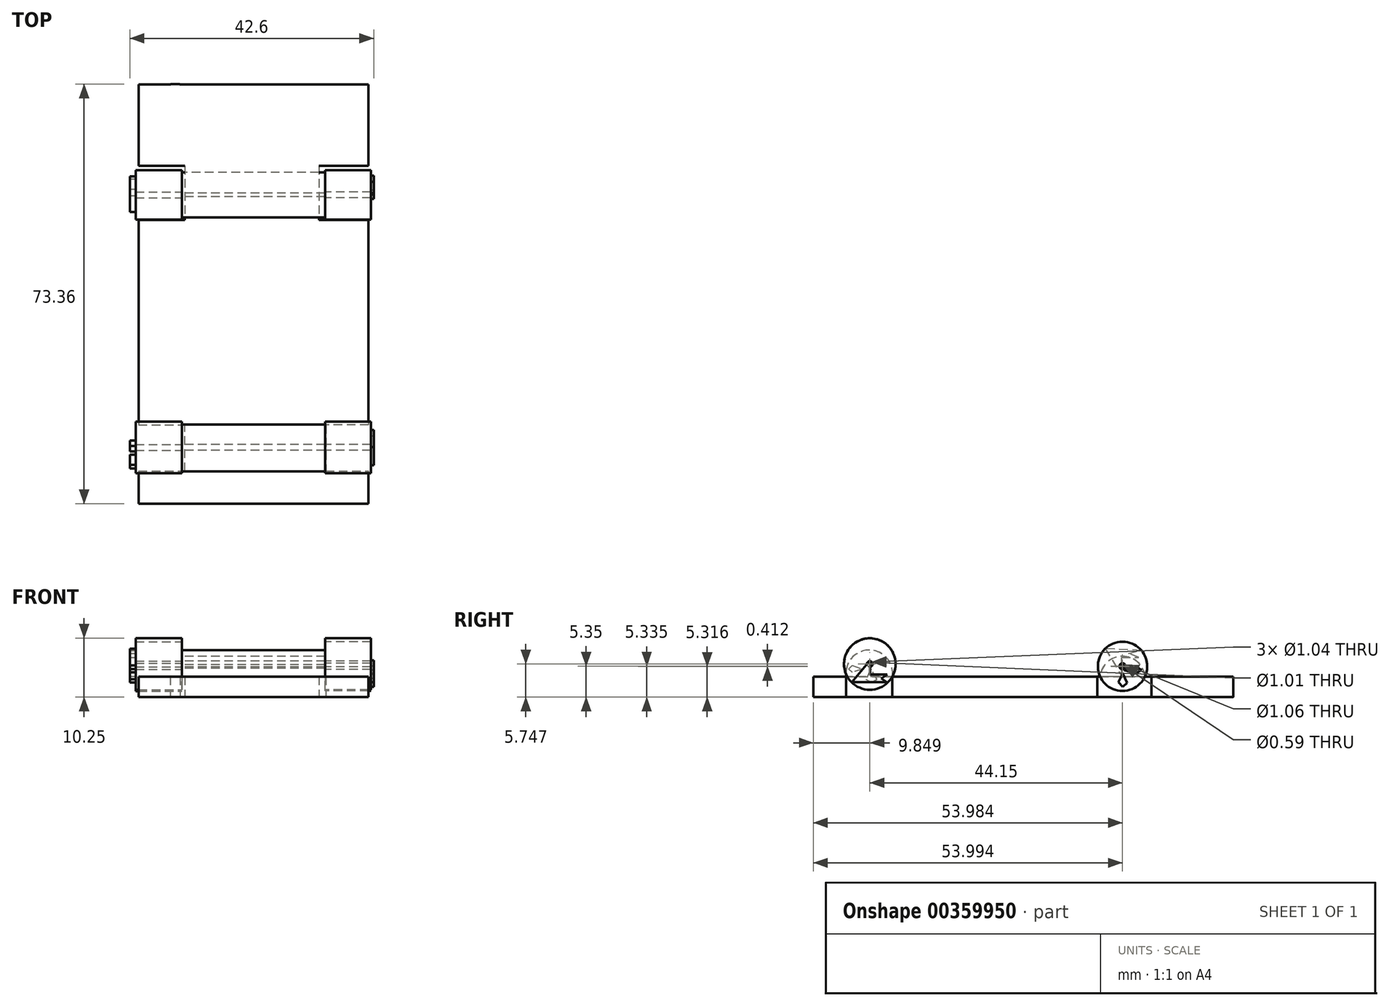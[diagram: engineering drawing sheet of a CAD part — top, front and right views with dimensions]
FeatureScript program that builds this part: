
annotation { "Feature Type Name" : "Feature", "Feature Type Description" : "" }
export const myFeature = defineFeature(function(context is Context, id is Id, definition is map)
    precondition{}
    {
        {
            var Q0;
            Q0=qCreatedBy(makeId("Top.planeOp"),FACE);
            var sketch = newSketch(context, id + "F0", { "sketchPlane" : qUnion([Q0])});
            skLineSegment(sketch, "E0.bottom", {"start": v(-14.53, 35.08) * mm, "end": v(14.97, 35.08) * mm});
            skLineSegment(sketch, "E0.top", {"start": v(-15.4, -38.23) * mm, "end": v(16.36, -38.23) * mm});
            skLineSegment(sketch, "E0.left", {"start": v(-20.07, 31.05) * mm, "end": v(-20.07, 20.84) * mm});
            skLineSegment(sketch, "E0.right", {"start": v(20.1, 30.52) * mm, "end": v(20.1, 20.84) * mm});
            skLineSegment(sketch, "E1", {"start": v(-20.07, 20.84) * mm, "end": v(-12.02, 20.84) * mm});
            skLineSegment(sketch, "E2", {"start": v(-12.02, 20.84) * mm, "end": v(-12.02, 11.39) * mm});
            skLineSegment(sketch, "E3", {"start": v(-20.07, 11.39) * mm, "end": v(-12.02, 11.39) * mm});
            skLineSegment(sketch, "E4", {"start": v(-20.07, -24.44) * mm, "end": v(-12.02, -24.44) * mm});
            skLineSegment(sketch, "E5", {"start": v(-12.02, -32.52) * mm, "end": v(-12.02, -24.44) * mm});
            skLineSegment(sketch, "E6", {"start": v(-20.07, -32.52) * mm, "end": v(-12.02, -32.52) * mm});
            skLineSegment(sketch, "E7", {"start": v(20.1, 20.84) * mm, "end": v(11.43, 20.84) * mm});
            skLineSegment(sketch, "E8", {"start": v(11.43, 20.84) * mm, "end": v(11.43, 11.39) * mm});
            skLineSegment(sketch, "E9", {"start": v(11.43, 11.39) * mm, "end": v(20.1, 11.39) * mm});
            skLineSegment(sketch, "E10", {"start": v(20.1, -24.44) * mm, "end": v(12.61, -24.44) * mm});
            skLineSegment(sketch, "E11", {"start": v(12.61, -24.44) * mm, "end": v(12.61, -32.52) * mm});
            skLineSegment(sketch, "E12", {"start": v(12.61, -32.52) * mm, "end": v(20.1, -32.52) * mm});
            skLineSegment(sketch, "E13.trimOffspring", {"start": v(-20.07, 11.39) * mm, "end": v(-20.07, -24.44) * mm});
            skLineSegment(sketch, "E14.trimOffspring", {"start": v(-20.07, -32.52) * mm, "end": v(-20.07, -35.37) * mm});
            skLineSegment(sketch, "E15.trimOffspring", {"start": v(20.1, -32.52) * mm, "end": v(20.1, -35.37) * mm});
            skLineSegment(sketch, "E16.trimOffspring", {"start": v(20.1, 11.39) * mm, "end": v(20.1, -24.44) * mm});
            skArc(sketch, "E17", {"start": v(-12.82, 35.08) * mm, "mid": v(-13.68, 35.13) * mm, "end": v(-14.53, 35.08) * mm});
            skPoint(sketch, "E18.startSnap0", {"position": v(16.36, -24.44) * mm});
            skPoint(sketch, "E19.orphan", {"position": v(-20.07, -38.23) * mm});
            skPoint(sketch, "E20.orphan", {"position": v(20.1, -38.23) * mm});
            skLineSegment(sketch, "E21", {"start": v(-20.07, 31.05) * mm, "end": v(-20.07, 35.08) * mm});
            skLineSegment(sketch, "E22", {"start": v(-20.07, 35.08) * mm, "end": v(-14.53, 35.08) * mm});
            skLineSegment(sketch, "E23", {"start": v(14.97, 35.08) * mm, "end": v(20.1, 35.08) * mm});
            skLineSegment(sketch, "E24", {"start": v(20.1, 35.08) * mm, "end": v(20.1, 30.52) * mm});
            skLineSegment(sketch, "E25", {"start": v(-20.07, -35.37) * mm, "end": v(-20.07, -38.23) * mm});
            skLineSegment(sketch, "E26", {"start": v(-20.07, -38.23) * mm, "end": v(-15.4, -38.23) * mm});
            skLineSegment(sketch, "E27", {"start": v(16.36, -38.23) * mm, "end": v(20.1, -38.23) * mm});
            skLineSegment(sketch, "E28", {"start": v(20.1, -35.37) * mm, "end": v(20.1, -38.23) * mm});
            skSolve(sketch);
        }
        {
            var Q0;
            Q0 = qSketchRegion(id + "F0", true);
            extrude(context, id + "F1", {"entities" : qUnion([Q0]), "depth" : 3.56 * mm});
        }
        {
            var Q0;
            Q0=qCreatedBy(makeId("Right.planeOp"),FACE);
            var sketch = newSketch(context, id + "F2", { "sketchPlane" : qUnion([Q0])});
            skArc(sketch, "E29", {"start": v(-24.43, 3.56) * mm, "mid": v(-28.47, 8.2) * mm, "end": v(-32.52, 3.56) * mm});
            skArc(sketch, "E30", {"start": v(19.7, 3.55) * mm, "mid": v(15.77, 7.1) * mm, "end": v(11.82, 3.56) * mm});
            skLineSegment(sketch, "E31", {"start": v(-32.52, 3.56) * mm, "end": v(-24.43, 3.56) * mm});
            skCircle(sketch, "E32", {"center": v(-28.38, 5.75) * mm, "radius": 0.52 * mm});
            skCircle(sketch, "E33", {"center": v(15.75, 5.32) * mm, "radius": 0.3 * mm});
            skLineSegment(sketch, "E34", {"start": v(11.82, 3.56) * mm, "end": v(19.7, 3.55) * mm});
            skSolve(sketch);
        }
        {
            var Q0;
            Q0 = qSketchRegion(id + "F2", true);
            extrude(context, id + "F3", {"entities" : qUnion([Q0]), "endBound" : BoundingType.SYMMETRIC, "depth" : 25 * mm});
        }
        {
            var Q0;
            Q0=makeQuery(id+"F3.opExtrude","CAP_FACE",FACE,{"disambiguationData":[OSD([sQuery(id+"F2.wireOp",EDGE,"E29"),sQuery(id+"F2.wireOp",EDGE,"E31"),sQuery(id+"F2.wireOp",EDGE,"E32")])],"isStart":false});
            var sketch = newSketch(context, id + "F4", { "sketchPlane" : qUnion([Q0])});
            skCircle(sketch, "E35", {"center": v(-28.38, 5.75) * mm, "radius": 4.5 * mm});
            skCircle(sketch, "E36", {"center": v(15.76, 5.35) * mm, "radius": 4.3 * mm});
            skCircle(sketch, "E37", {"center": v(-28.38, 5.75) * mm, "radius": 0.5 * mm});
            skCircle(sketch, "E38", {"center": v(15.76, 5.35) * mm, "radius": 0.53 * mm});
            skSolve(sketch);
        }
        {
            var Q0;
            Q0 = qSketchRegion(id + "F4", true);
            extrude(context, id + "F5", {"entities" : qUnion([Q0]), "depth" : 8 * mm});
        }
        {
            var Q0;
            Q0=makeQuery(id+"F3.opExtrude","CAP_FACE",FACE,{"disambiguationData":[OSD([sQuery(id+"F2.wireOp",EDGE,"E29"),sQuery(id+"F2.wireOp",EDGE,"E31"),sQuery(id+"F2.wireOp",EDGE,"E32")])],"isStart":true});
            var sketch = newSketch(context, id + "F6", { "sketchPlane" : qUnion([Q0])});
            skCircle(sketch, "E39", {"center": v(28.38, 5.75) * mm, "radius": 4.5 * mm});
            skCircle(sketch, "E40", {"center": v(-15.77, 5.34) * mm, "radius": 4.31 * mm});
            skCircle(sketch, "E41", {"center": v(-15.77, 5.34) * mm, "radius": 0.52 * mm});
            skCircle(sketch, "E42", {"center": v(28.38, 5.75) * mm, "radius": 0.52 * mm});
            skSolve(sketch);
        }
        {
            var Q0;
            Q0 = qSketchRegion(id + "F6", true);
            extrude(context, id + "F7", {"entities" : qUnion([Q0]), "depth" : 8.1 * mm});
        }
        {
            var Q0;
            Q0=makeQuery(id+"F7.opExtrude","CAP_FACE",FACE,{"disambiguationData":[OSD([sQuery(id+"F6.wireOp",EDGE,"E39")])],"isStart":false});
            var sketch = newSketch(context, id + "F8", { "sketchPlane" : qUnion([Q0])});
            skLineSegment(sketch, "E43", {"start": v(31.43, 4.28) * mm, "end": v(32.05, 4.86) * mm});
            skLineSegment(sketch, "E44", {"start": v(32.05, 4.86) * mm, "end": v(31.44, 5.5) * mm});
            skLineSegment(sketch, "E45", {"start": v(31.44, 5.5) * mm, "end": v(29.64, 4.86) * mm});
            skLineSegment(sketch, "E46", {"start": v(29.64, 4.86) * mm, "end": v(31.43, 4.28) * mm});
            skLineSegment(sketch, "E47", {"start": v(28.13, 4.86) * mm, "end": v(29.1, 3.07) * mm});
            skLineSegment(sketch, "E48", {"start": v(29.1, 3.07) * mm, "end": v(28.07, 2.5) * mm});
            skLineSegment(sketch, "E49", {"start": v(28.07, 2.5) * mm, "end": v(27.15, 3.07) * mm});
            skLineSegment(sketch, "E50", {"start": v(27.15, 3.07) * mm, "end": v(28.13, 4.86) * mm});
            skLineSegment(sketch, "E51", {"start": v(-18.99, 8.14) * mm, "end": v(-12.76, 8.42) * mm});
            skLineSegment(sketch, "E52", {"start": v(-12.76, 8.42) * mm, "end": v(-15.63, 3.6) * mm});
            skLineSegment(sketch, "E53", {"start": v(-15.63, 3.6) * mm, "end": v(-15.63, 6.9) * mm});
            skLineSegment(sketch, "E54", {"start": v(-15.63, 6.9) * mm, "end": v(-18.58, 6.9) * mm});
            skLineSegment(sketch, "E55", {"start": v(-18.58, 6.9) * mm, "end": v(-16.8, 7.62) * mm});
            skLineSegment(sketch, "E56", {"start": v(-16.8, 7.62) * mm, "end": v(-18.99, 8.14) * mm});
            skSolve(sketch);
        }
        {
            var Q0;
            Q0 = qSketchRegion(id + "F8", true);
            extrude(context, id + "F9", {"entities" : qUnion([Q0]), "depth" : 1 * mm});
        }
        {
            var Q0;
            Q0=makeQuery(id+"F5.opExtrude","CAP_FACE",FACE,{"disambiguationData":[OSD([sQuery(id+"F4.wireOp",EDGE,"E36")])],"isStart":false});
            var sketch = newSketch(context, id + "F10", { "sketchPlane" : qUnion([Q0])});
            skLineSegment(sketch, "E57", {"start": v(18.05, 4.12) * mm, "end": v(19.13, 4.65) * mm});
            skLineSegment(sketch, "E58", {"start": v(19.13, 4.65) * mm, "end": v(18.07, 5.4) * mm});
            skLineSegment(sketch, "E59", {"start": v(18.07, 5.4) * mm, "end": v(16.07, 4.65) * mm});
            skLineSegment(sketch, "E60", {"start": v(16.07, 4.65) * mm, "end": v(18.05, 4.12) * mm});
            skLineSegment(sketch, "E61", {"start": v(15.83, 1.76) * mm, "end": v(16.56, 2.45) * mm});
            skLineSegment(sketch, "E62", {"start": v(16.56, 2.45) * mm, "end": v(15.83, 4.12) * mm});
            skLineSegment(sketch, "E63", {"start": v(15.83, 4.12) * mm, "end": v(15.05, 2.55) * mm});
            skLineSegment(sketch, "E64", {"start": v(15.05, 2.55) * mm, "end": v(15.83, 1.76) * mm});
            skLineSegment(sketch, "E65", {"start": v(-25.38, 2.55) * mm, "end": v(-31.48, 2.55) * mm});
            skLineSegment(sketch, "E66", {"start": v(-31.48, 2.55) * mm, "end": v(-28.34, 6.38) * mm});
            skLineSegment(sketch, "E67", {"start": v(-28.34, 6.38) * mm, "end": v(-28.34, 3.9) * mm});
            skLineSegment(sketch, "E68", {"start": v(-28.34, 3.9) * mm, "end": v(-25.34, 3.9) * mm});
            skLineSegment(sketch, "E69", {"start": v(-25.34, 3.9) * mm, "end": v(-26.38, 3.22) * mm});
            skLineSegment(sketch, "E70", {"start": v(-26.38, 3.22) * mm, "end": v(-25.38, 2.55) * mm});
            skSolve(sketch);
        }
        {
            var Q0;
            Q0 = qSketchRegion(id + "F10", true);
            extrude(context, id + "F11", {"entities" : qUnion([Q0]), "depth" : 0.5 * mm});
        }
    });
